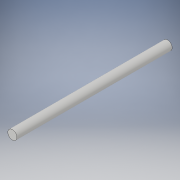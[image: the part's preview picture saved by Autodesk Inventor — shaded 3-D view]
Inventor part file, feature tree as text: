
AUTODESK INVENTOR PART (.ipt)
format: ipt  version: 2017 (Build 210142000, 142)  size: 89,600 bytes
history: native  units: in
note: dims shown in document units (in); Inventor stores cm internally (conversion verified against a paired STEP export)
features: extrude x1, sketch x1
ambient origin geometry x8: Origin, YZ Plane, XZ Plane, XY Plane, X Axis, Y Axis, Z Axis, Center Point
bodies: Solid1 (feature_tree)
feature tree (2):
  extrude  "Extrusion1"  Depth=4.0in TaperAngle=0.0deg
  sketch  "Sketch1"  dims[d0=0.236in d1=4.0in d2=0.0in]
